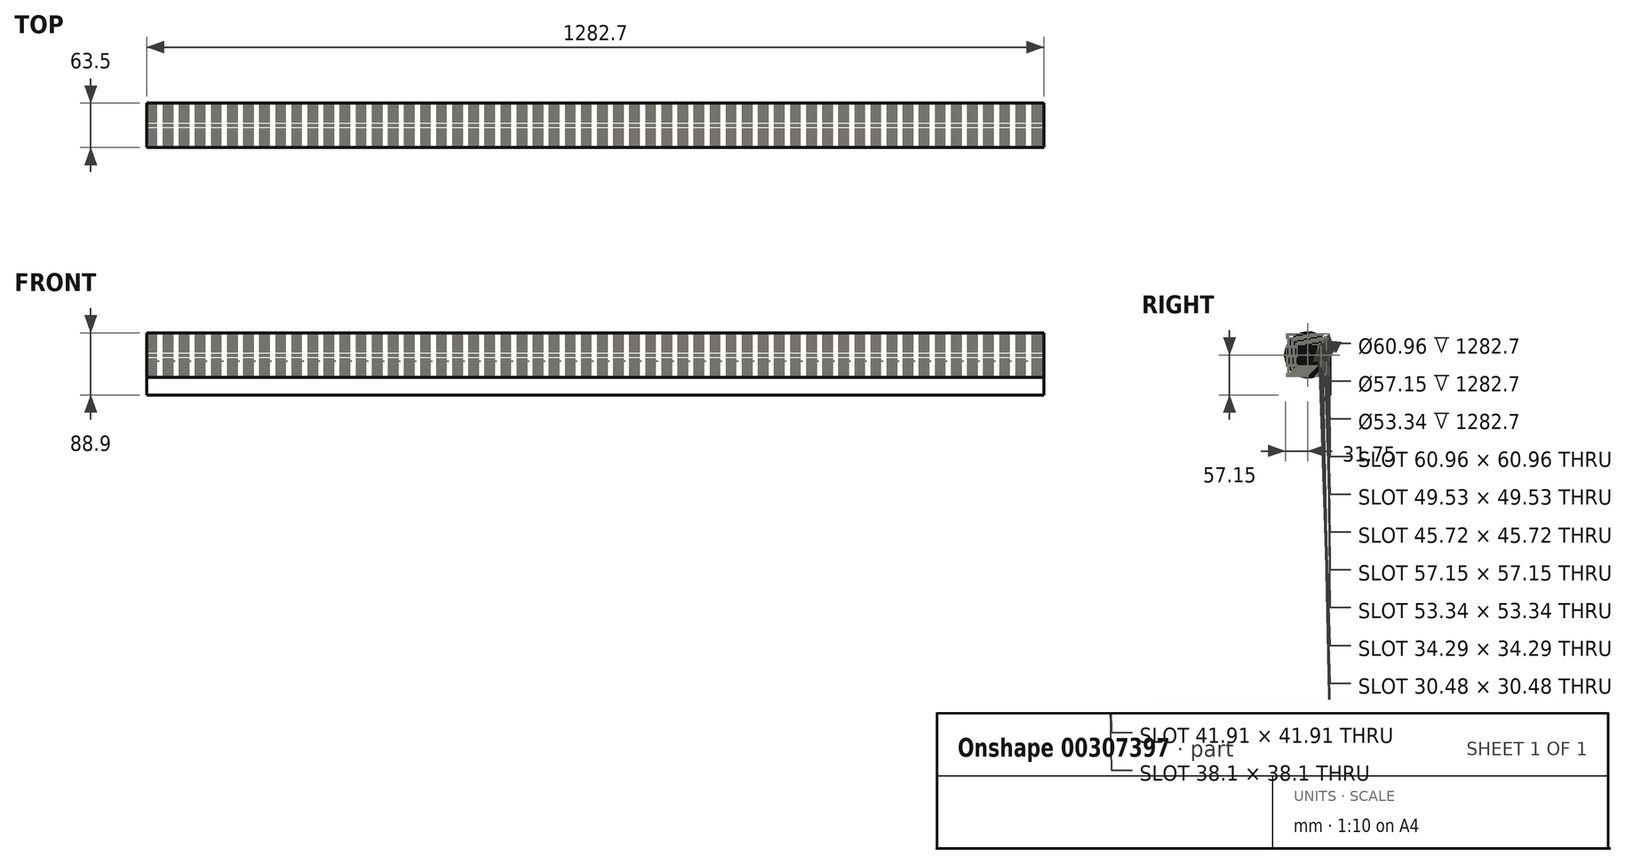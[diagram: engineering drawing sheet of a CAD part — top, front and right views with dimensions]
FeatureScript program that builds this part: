
annotation { "Feature Type Name" : "Feature", "Feature Type Description" : "" }
export const myFeature = defineFeature(function(context is Context, id is Id, definition is map)
    precondition{}
    {
        {
            var Q0;
            Q0=qCreatedBy(makeId("Right.planeOp"),FACE);
            var sketch = newSketch(context, id + "F0", { "sketchPlane" : qUnion([Q0])});
            skLineSegment(sketch, "E0", {"start": v(0, 0) * mm, "end": v(-1.27, 0) * mm});
            skLineSegment(sketch, "E1", {"start": v(-1.27, 0) * mm, "end": v(-1.27, 52.07) * mm});
            skLineSegment(sketch, "E2", {"start": v(0, 0) * mm, "end": v(0, 57.15) * mm});
            skLineSegment(sketch, "E3", {"start": v(-1.27, 52.07) * mm, "end": v(-1.27, 57.15) * mm});
            skLineSegment(sketch, "E4", {"start": v(-1.27, 57.15) * mm, "end": v(0, 57.15) * mm});
            skSolve(sketch);
        }
        {
            var Q0;
            Q0=qSketchRegion(id+"F0",true);
            extrude(context, id + "F1", {"entities" : qUnion([Q0]), "endBound" : BoundingType.SYMMETRIC, "depth" : 1282.7 * mm});
        }
        {
            var Q0;
            Q0=qCreatedBy(makeId("Right.planeOp"),FACE);
            var sketch = newSketch(context, id + "F2", { "sketchPlane" : qUnion([Q0])});
            skCircle(sketch, "E5", {"center": v(-31.75, 57.15) * mm, "radius": 31.75 * mm});
            skPoint(sketch, "E5.first.point", {"position": v(0, 57.15) * mm});
            skPoint(sketch, "E5.second.point", {"position": v(0, 57.15) * mm});
            skPoint(sketch, "E5.third.point", {"position": v(0, 57.15) * mm});
            skSolve(sketch);
        }
        {
            var Q0;
            Q0=makeQuery(id+"F2.imprint","IMPRINT",FACE,{"disambiguationData":[TD([[makeQuery(id+"F2.imprint","IMPRINT",EDGE,{"derivedFrom":sQuery(id+"F2.wireOp",EDGE,"E5")}),1.0]])]});
            var Q1;
            Q1=makeQuery(id+"F1.opExtrude","CAP_FACE",FACE,{"disambiguationData":[OSD([sQuery(id+"F0.wireOp",EDGE,"E0"),sQuery(id+"F0.wireOp",EDGE,"E1"),sQuery(id+"F0.wireOp",EDGE,"E2"),sQuery(id+"F0.wireOp",EDGE,"E3"),sQuery(id+"F0.wireOp",EDGE,"E4")])],"isStart":false});
            var Q2;
            Q2=makeQuery(id+"F1.opExtrude","CAP_FACE",FACE,{"disambiguationData":[OSD([sQuery(id+"F0.wireOp",EDGE,"E0"),sQuery(id+"F0.wireOp",EDGE,"E1"),sQuery(id+"F0.wireOp",EDGE,"E2"),sQuery(id+"F0.wireOp",EDGE,"E3"),sQuery(id+"F0.wireOp",EDGE,"E4")])],"isStart":true});
            extrude(context, id + "F3", {"entities" : qUnion([Q0]), "operationType" : NewBodyOperationType.ADD, "endBound" : BoundingType.UP_TO_SURFACE, "endBoundEntityFace" : qUnion([Q1]), "depth" : 25.4 * mm, "hasSecondDirection" : true, "secondDirectionBound" : SecondDirectionBoundingType.UP_TO_SURFACE, "secondDirectionOppositeDirection" : true, "secondDirectionBoundEntityFace" : qUnion([Q2]), "secondDirectionDepth" : 25.4 * mm});
        }
        {
            var Q0;
            Q0=makeQuery(id+"F3.boolean.opBoolean","MERGE",FACE,{"derivedFrom":[makeQuery(id+"F1.opExtrude","CAP_FACE",FACE,{"disambiguationData":[OSD([sQuery(id+"F0.wireOp",EDGE,"E0"),sQuery(id+"F0.wireOp",EDGE,"E1"),sQuery(id+"F0.wireOp",EDGE,"E2"),sQuery(id+"F0.wireOp",EDGE,"E3"),sQuery(id+"F0.wireOp",EDGE,"E4")])],"isStart":false}),makeQuery(id+"F3.opExtrude","CAP_FACE",FACE,{"disambiguationData":[OSD([sQuery(id+"F2.wireOp",EDGE,"E5")])],"isStart":false})]});
            var sketch = newSketch(context, id + "F4", { "sketchPlane" : qUnion([Q0])});
            skCircle(sketch, "E6", {"center": v(-31.75, 57.15) * mm, "radius": 30.48 * mm});
            skCircle(sketch, "E7", {"center": v(-31.75, 57.15) * mm, "radius": 29.84 * mm});
            skCircle(sketch, "E8", {"center": v(-31.75, 57.15) * mm, "radius": 28.58 * mm});
            skLineSegment(sketch, "E9", {"start": v(-62.23, 57.15) * mm, "end": v(-63.5, 57.15) * mm, "construction": true});
            skLineSegment(sketch, "E10", {"start": v(-31.75, 57.15) * mm, "end": v(-33.02, 57.15) * mm, "construction": true});
            skLineSegment(sketch, "E11", {"start": v(-60.33, 57.15) * mm, "end": v(-61.6, 57.15) * mm, "construction": true});
            skLineSegment(sketch, "E12", {"start": v(-61.6, 57.15) * mm, "end": v(-62.23, 57.15) * mm, "construction": true});
            skLineSegment(sketch, "E13", {"start": v(-1.27, 38.17) * mm, "end": v(0, 38.17) * mm, "construction": true});
            skCircle(sketch, "E14", {"center": v(-31.75, 57.15) * mm, "radius": 27.94 * mm});
            skCircle(sketch, "E15", {"center": v(-31.75, 57.15) * mm, "radius": 26.67 * mm});
            skCircle(sketch, "E16", {"center": v(-31.75, 57.15) * mm, "radius": 26.03 * mm});
            skCircle(sketch, "E17", {"center": v(-31.75, 57.15) * mm, "radius": 24.76 * mm});
            skLineSegment(sketch, "E18", {"start": v(-33.02, 57.15) * mm, "end": v(-56.51, 57.15) * mm, "construction": true});
            skLineSegment(sketch, "E19", {"start": v(-56.51, 57.15) * mm, "end": v(-57.78, 57.15) * mm, "construction": true});
            skLineSegment(sketch, "E20", {"start": v(-57.78, 57.15) * mm, "end": v(-58.42, 57.15) * mm, "construction": true});
            skLineSegment(sketch, "E21", {"start": v(-58.42, 57.15) * mm, "end": v(-59.69, 57.15) * mm, "construction": true});
            skLineSegment(sketch, "E22", {"start": v(-59.69, 57.15) * mm, "end": v(-60.33, 57.15) * mm, "construction": true});
            skLineSegment(sketch, "E23", {"start": v(-62.23, 57.14) * mm, "end": v(-61.6, 57.14) * mm});
            skLineSegment(sketch, "E24", {"start": v(-61.6, 57.14) * mm, "end": v(-60.32, 57.14) * mm});
            skLineSegment(sketch, "E25", {"start": v(-60.32, 57.14) * mm, "end": v(-59.69, 57.14) * mm});
            skLineSegment(sketch, "E26", {"start": v(-59.69, 57.14) * mm, "end": v(-58.42, 57.14) * mm});
            skLineSegment(sketch, "E27", {"start": v(-58.42, 57.14) * mm, "end": v(-57.78, 57.14) * mm});
            skLineSegment(sketch, "E28", {"start": v(-57.78, 57.14) * mm, "end": v(-56.51, 57.14) * mm});
            skLineSegment(sketch, "E29", {"start": v(-56.51, 57.16) * mm, "end": v(-57.78, 57.16) * mm});
            skLineSegment(sketch, "E30", {"start": v(-57.78, 57.16) * mm, "end": v(-58.42, 57.16) * mm});
            skLineSegment(sketch, "E31", {"start": v(-58.42, 57.16) * mm, "end": v(-59.69, 57.16) * mm});
            skLineSegment(sketch, "E32", {"start": v(-59.69, 57.16) * mm, "end": v(-60.32, 57.16) * mm});
            skLineSegment(sketch, "E33", {"start": v(-60.32, 57.16) * mm, "end": v(-61.6, 57.16) * mm});
            skLineSegment(sketch, "E34", {"start": v(-61.6, 57.16) * mm, "end": v(-62.23, 57.16) * mm});
            skLineSegment(sketch, "E35.1.0.0", {"start": v(-55.88, 57.16) * mm, "end": v(-56.51, 57.16) * mm});
            skLineSegment(sketch, "E35.1.0.1", {"start": v(-55.88, 57.15) * mm, "end": v(-56.51, 57.15) * mm, "construction": true});
            skLineSegment(sketch, "E35.1.0.2", {"start": v(-56.51, 57.14) * mm, "end": v(-55.88, 57.14) * mm});
            skLineSegment(sketch, "E35.1.0.4", {"start": v(-55.88, 57.14) * mm, "end": v(-54.6, 57.14) * mm});
            skLineSegment(sketch, "E35.1.0.5", {"start": v(-54.6, 57.15) * mm, "end": v(-55.88, 57.15) * mm, "construction": true});
            skLineSegment(sketch, "E35.1.0.6", {"start": v(-54.6, 57.16) * mm, "end": v(-55.88, 57.16) * mm});
            skLineSegment(sketch, "E35.2.0.0", {"start": v(-53.97, 57.16) * mm, "end": v(-54.6, 57.16) * mm});
            skLineSegment(sketch, "E35.2.0.1", {"start": v(-53.97, 57.15) * mm, "end": v(-54.6, 57.15) * mm, "construction": true});
            skLineSegment(sketch, "E35.2.0.2", {"start": v(-54.6, 57.14) * mm, "end": v(-53.97, 57.14) * mm});
            skLineSegment(sketch, "E35.2.0.4", {"start": v(-53.97, 57.14) * mm, "end": v(-52.7, 57.14) * mm});
            skLineSegment(sketch, "E35.2.0.5", {"start": v(-52.7, 57.15) * mm, "end": v(-53.97, 57.15) * mm, "construction": true});
            skLineSegment(sketch, "E35.2.0.6", {"start": v(-52.7, 57.16) * mm, "end": v(-53.97, 57.16) * mm});
            skLineSegment(sketch, "E35.3.0.0", {"start": v(-52.07, 57.16) * mm, "end": v(-52.7, 57.16) * mm});
            skLineSegment(sketch, "E35.3.0.1", {"start": v(-52.07, 57.15) * mm, "end": v(-52.7, 57.15) * mm, "construction": true});
            skLineSegment(sketch, "E35.3.0.2", {"start": v(-52.7, 57.14) * mm, "end": v(-52.07, 57.14) * mm});
            skLineSegment(sketch, "E35.3.0.4", {"start": v(-52.07, 57.14) * mm, "end": v(-50.8, 57.14) * mm});
            skLineSegment(sketch, "E35.3.0.5", {"start": v(-50.8, 57.15) * mm, "end": v(-52.07, 57.15) * mm, "construction": true});
            skLineSegment(sketch, "E35.3.0.6", {"start": v(-50.8, 57.16) * mm, "end": v(-52.07, 57.16) * mm});
            skLineSegment(sketch, "E35.4.0.0", {"start": v(-50.16, 57.16) * mm, "end": v(-50.8, 57.16) * mm});
            skLineSegment(sketch, "E35.4.0.1", {"start": v(-50.16, 57.15) * mm, "end": v(-50.8, 57.15) * mm, "construction": true});
            skLineSegment(sketch, "E35.4.0.2", {"start": v(-50.8, 57.14) * mm, "end": v(-50.16, 57.14) * mm});
            skLineSegment(sketch, "E35.4.0.4", {"start": v(-50.16, 57.14) * mm, "end": v(-48.9, 57.14) * mm});
            skLineSegment(sketch, "E35.4.0.5", {"start": v(-48.9, 57.15) * mm, "end": v(-50.16, 57.15) * mm, "construction": true});
            skLineSegment(sketch, "E35.4.0.6", {"start": v(-48.9, 57.16) * mm, "end": v(-50.16, 57.16) * mm});
            skLineSegment(sketch, "E35.5.0.0", {"start": v(-48.26, 57.16) * mm, "end": v(-48.9, 57.16) * mm});
            skLineSegment(sketch, "E35.5.0.1", {"start": v(-48.26, 57.15) * mm, "end": v(-48.9, 57.15) * mm, "construction": true});
            skLineSegment(sketch, "E35.5.0.2", {"start": v(-48.9, 57.14) * mm, "end": v(-48.26, 57.14) * mm});
            skLineSegment(sketch, "E35.5.0.4", {"start": v(-48.26, 57.14) * mm, "end": v(-46.99, 57.14) * mm});
            skLineSegment(sketch, "E35.5.0.5", {"start": v(-46.99, 57.15) * mm, "end": v(-48.26, 57.15) * mm, "construction": true});
            skLineSegment(sketch, "E35.5.0.6", {"start": v(-46.99, 57.16) * mm, "end": v(-48.26, 57.16) * mm});
            skLineSegment(sketch, "E35.6.0.0", {"start": v(-46.35, 57.16) * mm, "end": v(-46.99, 57.16) * mm});
            skLineSegment(sketch, "E35.6.0.1", {"start": v(-46.35, 57.15) * mm, "end": v(-47, 57.15) * mm, "construction": true});
            skLineSegment(sketch, "E35.6.0.2", {"start": v(-46.99, 57.14) * mm, "end": v(-46.35, 57.14) * mm});
            skLineSegment(sketch, "E35.6.0.4", {"start": v(-46.35, 57.14) * mm, "end": v(-45.08, 57.14) * mm});
            skLineSegment(sketch, "E35.6.0.5", {"start": v(-45.08, 57.15) * mm, "end": v(-46.35, 57.15) * mm, "construction": true});
            skLineSegment(sketch, "E35.6.0.6", {"start": v(-45.08, 57.16) * mm, "end": v(-46.35, 57.16) * mm});
            skLineSegment(sketch, "E35.7.0.0", {"start": v(-44.45, 57.16) * mm, "end": v(-45.08, 57.16) * mm});
            skLineSegment(sketch, "E35.7.0.1", {"start": v(-44.45, 57.15) * mm, "end": v(-45.09, 57.15) * mm, "construction": true});
            skLineSegment(sketch, "E35.7.0.2", {"start": v(-45.08, 57.14) * mm, "end": v(-44.45, 57.14) * mm});
            skLineSegment(sketch, "E35.7.0.4", {"start": v(-44.45, 57.14) * mm, "end": v(-43.18, 57.14) * mm});
            skLineSegment(sketch, "E35.7.0.5", {"start": v(-43.18, 57.15) * mm, "end": v(-44.45, 57.15) * mm, "construction": true});
            skLineSegment(sketch, "E35.7.0.6", {"start": v(-43.18, 57.16) * mm, "end": v(-44.45, 57.16) * mm});
            skLineSegment(sketch, "E35.8.0.0", {"start": v(-42.54, 57.16) * mm, "end": v(-43.18, 57.16) * mm});
            skLineSegment(sketch, "E35.8.0.1", {"start": v(-42.55, 57.15) * mm, "end": v(-43.18, 57.15) * mm, "construction": true});
            skLineSegment(sketch, "E35.8.0.2", {"start": v(-43.18, 57.14) * mm, "end": v(-42.54, 57.14) * mm});
            skLineSegment(sketch, "E35.8.0.4", {"start": v(-42.54, 57.14) * mm, "end": v(-41.27, 57.14) * mm});
            skLineSegment(sketch, "E35.8.0.5", {"start": v(-41.27, 57.15) * mm, "end": v(-42.55, 57.15) * mm, "construction": true});
            skLineSegment(sketch, "E35.8.0.6", {"start": v(-41.27, 57.16) * mm, "end": v(-42.54, 57.16) * mm});
            skLineSegment(sketch, "E35.9.0.0", {"start": v(-40.64, 57.16) * mm, "end": v(-41.27, 57.16) * mm});
            skLineSegment(sketch, "E35.9.0.1", {"start": v(-40.64, 57.15) * mm, "end": v(-41.28, 57.15) * mm, "construction": true});
            skLineSegment(sketch, "E35.9.0.2", {"start": v(-41.27, 57.14) * mm, "end": v(-40.64, 57.14) * mm});
            skLineSegment(sketch, "E35.9.0.4", {"start": v(-40.64, 57.14) * mm, "end": v(-39.37, 57.14) * mm});
            skLineSegment(sketch, "E35.9.0.5", {"start": v(-39.37, 57.15) * mm, "end": v(-40.64, 57.15) * mm, "construction": true});
            skLineSegment(sketch, "E35.9.0.6", {"start": v(-39.37, 57.16) * mm, "end": v(-40.64, 57.16) * mm});
            skLineSegment(sketch, "E35.10.0.0", {"start": v(-38.73, 57.16) * mm, "end": v(-39.37, 57.16) * mm});
            skLineSegment(sketch, "E35.10.0.1", {"start": v(-38.74, 57.15) * mm, "end": v(-39.37, 57.15) * mm, "construction": true});
            skLineSegment(sketch, "E35.10.0.2", {"start": v(-39.37, 57.14) * mm, "end": v(-38.73, 57.14) * mm});
            skLineSegment(sketch, "E35.10.0.4", {"start": v(-38.73, 57.14) * mm, "end": v(-37.46, 57.14) * mm});
            skLineSegment(sketch, "E35.10.0.5", {"start": v(-37.47, 57.15) * mm, "end": v(-38.74, 57.15) * mm, "construction": true});
            skLineSegment(sketch, "E35.10.0.6", {"start": v(-37.46, 57.16) * mm, "end": v(-38.73, 57.16) * mm});
            skLineSegment(sketch, "E35.11.0.0", {"start": v(-36.83, 57.16) * mm, "end": v(-37.46, 57.16) * mm});
            skLineSegment(sketch, "E35.11.0.1", {"start": v(-36.83, 57.15) * mm, "end": v(-37.47, 57.15) * mm, "construction": true});
            skLineSegment(sketch, "E35.11.0.2", {"start": v(-37.46, 57.14) * mm, "end": v(-36.83, 57.14) * mm});
            skLineSegment(sketch, "E35.11.0.4", {"start": v(-36.83, 57.14) * mm, "end": v(-35.56, 57.14) * mm});
            skLineSegment(sketch, "E35.11.0.5", {"start": v(-35.56, 57.15) * mm, "end": v(-36.83, 57.15) * mm, "construction": true});
            skLineSegment(sketch, "E35.11.0.6", {"start": v(-35.56, 57.16) * mm, "end": v(-36.83, 57.16) * mm});
            skLineSegment(sketch, "E35.direction1", {"start": v(-58.42, 57.14) * mm, "end": v(-56.51, 57.14) * mm, "construction": true});
            skCircle(sketch, "E36", {"center": v(-31.75, 57.15) * mm, "radius": 24.13 * mm});
            skCircle(sketch, "E37", {"center": v(-31.75, 57.15) * mm, "radius": 22.86 * mm});
            skCircle(sketch, "E38", {"center": v(-31.75, 57.15) * mm, "radius": 22.23 * mm});
            skCircle(sketch, "E39", {"center": v(-31.75, 57.15) * mm, "radius": 20.96 * mm});
            skCircle(sketch, "E40", {"center": v(-31.75, 57.15) * mm, "radius": 20.32 * mm});
            skCircle(sketch, "E41", {"center": v(-31.75, 57.15) * mm, "radius": 19.05 * mm});
            skCircle(sketch, "E42", {"center": v(-31.75, 57.15) * mm, "radius": 18.42 * mm});
            skCircle(sketch, "E43", {"center": v(-31.75, 57.15) * mm, "radius": 17.15 * mm});
            skCircle(sketch, "E44", {"center": v(-31.75, 57.15) * mm, "radius": 16.51 * mm});
            skCircle(sketch, "E45", {"center": v(-31.75, 57.15) * mm, "radius": 15.24 * mm});
            skCircle(sketch, "E46", {"center": v(-31.75, 57.15) * mm, "radius": 14.6 * mm});
            skCircle(sketch, "E47", {"center": v(-31.75, 57.15) * mm, "radius": 13.34 * mm});
            skCircle(sketch, "E48", {"center": v(-31.75, 57.15) * mm, "radius": 12.7 * mm});
            skCircle(sketch, "E49", {"center": v(-31.75, 57.15) * mm, "radius": 11.43 * mm});
            skCircle(sketch, "E50", {"center": v(-31.75, 57.15) * mm, "radius": 10.8 * mm});
            skCircle(sketch, "E51", {"center": v(-31.75, 57.15) * mm, "radius": 9.53 * mm});
            skCircle(sketch, "E52", {"center": v(-31.75, 57.15) * mm, "radius": 8.9 * mm});
            skCircle(sketch, "E53", {"center": v(-31.75, 57.15) * mm, "radius": 7.62 * mm});
            skCircle(sketch, "E54", {"center": v(-31.75, 57.15) * mm, "radius": 6.99 * mm});
            skCircle(sketch, "E55", {"center": v(-31.75, 57.15) * mm, "radius": 5.72 * mm});
            skCircle(sketch, "E56", {"center": v(-31.75, 57.15) * mm, "radius": 5.08 * mm});
            skCircle(sketch, "E57", {"center": v(-31.75, 57.15) * mm, "radius": 3.81 * mm});
            skCircle(sketch, "E58", {"center": v(-31.75, 57.15) * mm, "radius": 1.27 * mm});
            skSolve(sketch);
        }
        {
            var Q0;
            {var subQ0=sQuery(id+"F4.wireOp",EDGE,"E23");Q0=makeQuery(id+"F4.imprint","IMPRINT",FACE,{"disambiguationData":[TD([[makeQuery(id+"F4.imprint","IMPRINT",EDGE,{"derivedFrom":subQ0}),-1.0]])]});}
            var Q1;
            {var subQ0=sQuery(id+"F4.wireOp",EDGE,"E25");Q1=makeQuery(id+"F4.imprint","IMPRINT",FACE,{"disambiguationData":[TD([[makeQuery(id+"F4.imprint","IMPRINT",EDGE,{"derivedFrom":subQ0}),-1.0]])]});}
            var Q2;
            {var subQ0=sQuery(id+"F4.wireOp",EDGE,"E27");Q2=makeQuery(id+"F4.imprint","IMPRINT",FACE,{"disambiguationData":[TD([[makeQuery(id+"F4.imprint","IMPRINT",EDGE,{"derivedFrom":subQ0}),-1.0]])]});}
            var Q3;
            {var subQ2=sQuery(id+"F4.wireOp",EDGE,"E35.1.0.0");Q3=makeQuery(id+"F4.imprint","IMPRINT",FACE,{"disambiguationData":[TD([[makeQuery(id+"F4.imprint","IMPRINT",EDGE,{"derivedFrom":subQ2}),-1.0]])]});}
            var Q4;
            {var subQ0=sQuery(id+"F4.wireOp",EDGE,"E35.2.0.0");Q4=makeQuery(id+"F4.imprint","IMPRINT",FACE,{"disambiguationData":[TD([[makeQuery(id+"F4.imprint","IMPRINT",EDGE,{"derivedFrom":subQ0}),-1.0]])]});}
            var Q5;
            {var subQ0=sQuery(id+"F4.wireOp",EDGE,"E35.3.0.0");Q5=makeQuery(id+"F4.imprint","IMPRINT",FACE,{"disambiguationData":[TD([[makeQuery(id+"F4.imprint","IMPRINT",EDGE,{"derivedFrom":subQ0}),-1.0]])]});}
            var Q6;
            {var subQ0=sQuery(id+"F4.wireOp",EDGE,"E35.4.0.0");Q6=makeQuery(id+"F4.imprint","IMPRINT",FACE,{"disambiguationData":[TD([[makeQuery(id+"F4.imprint","IMPRINT",EDGE,{"derivedFrom":subQ0}),-1.0]])]});}
            var Q7;
            {var subQ0=sQuery(id+"F4.wireOp",EDGE,"E35.5.0.0");Q7=makeQuery(id+"F4.imprint","IMPRINT",FACE,{"disambiguationData":[TD([[makeQuery(id+"F4.imprint","IMPRINT",EDGE,{"derivedFrom":subQ0}),-1.0]])]});}
            var Q8;
            {var subQ0=sQuery(id+"F4.wireOp",EDGE,"E35.6.0.0");Q8=makeQuery(id+"F4.imprint","IMPRINT",FACE,{"disambiguationData":[TD([[makeQuery(id+"F4.imprint","IMPRINT",EDGE,{"derivedFrom":subQ0}),-1.0]])]});}
            var Q9;
            {var subQ0=sQuery(id+"F4.wireOp",EDGE,"E35.7.0.0");Q9=makeQuery(id+"F4.imprint","IMPRINT",FACE,{"disambiguationData":[TD([[makeQuery(id+"F4.imprint","IMPRINT",EDGE,{"derivedFrom":subQ0}),-1.0]])]});}
            var Q10;
            {var subQ0=sQuery(id+"F4.wireOp",EDGE,"E35.8.0.0");Q10=makeQuery(id+"F4.imprint","IMPRINT",FACE,{"disambiguationData":[TD([[makeQuery(id+"F4.imprint","IMPRINT",EDGE,{"derivedFrom":subQ0}),-1.0]])]});}
            var Q11;
            {var subQ0=sQuery(id+"F4.wireOp",EDGE,"E35.9.0.0");Q11=makeQuery(id+"F4.imprint","IMPRINT",FACE,{"disambiguationData":[TD([[makeQuery(id+"F4.imprint","IMPRINT",EDGE,{"derivedFrom":subQ0}),-1.0]])]});}
            var Q12;
            {var subQ0=sQuery(id+"F4.wireOp",EDGE,"E35.10.0.0");Q12=makeQuery(id+"F4.imprint","IMPRINT",FACE,{"disambiguationData":[TD([[makeQuery(id+"F4.imprint","IMPRINT",EDGE,{"derivedFrom":subQ0}),-1.0]])]});}
            var Q13;
            {var subQ0=sQuery(id+"F4.wireOp",EDGE,"E35.11.0.0");Q13=makeQuery(id+"F4.imprint","IMPRINT",FACE,{"disambiguationData":[TD([[makeQuery(id+"F4.imprint","IMPRINT",EDGE,{"derivedFrom":subQ0}),-1.0]])]});}
            var Q14;
            Q14=makeQuery(id+"F4.imprint","IMPRINT",FACE,{"disambiguationData":[TD([[makeQuery(id+"F4.imprint","IMPRINT",EDGE,{"derivedFrom":sQuery(id+"F4.wireOp",EDGE,"E58")}),1.0]])]});
            extrude(context, id + "F5", {"entities" : qUnion([Q0, Q1, Q2, Q3, Q4, Q5, Q6, Q7, Q8, Q9, Q10, Q11, Q12, Q13, Q14]), "operationType" : NewBodyOperationType.REMOVE, "endBound" : BoundingType.THROUGH_ALL, "oppositeDirection" : true, "depth" : 25.4 * mm});
        }
    });
